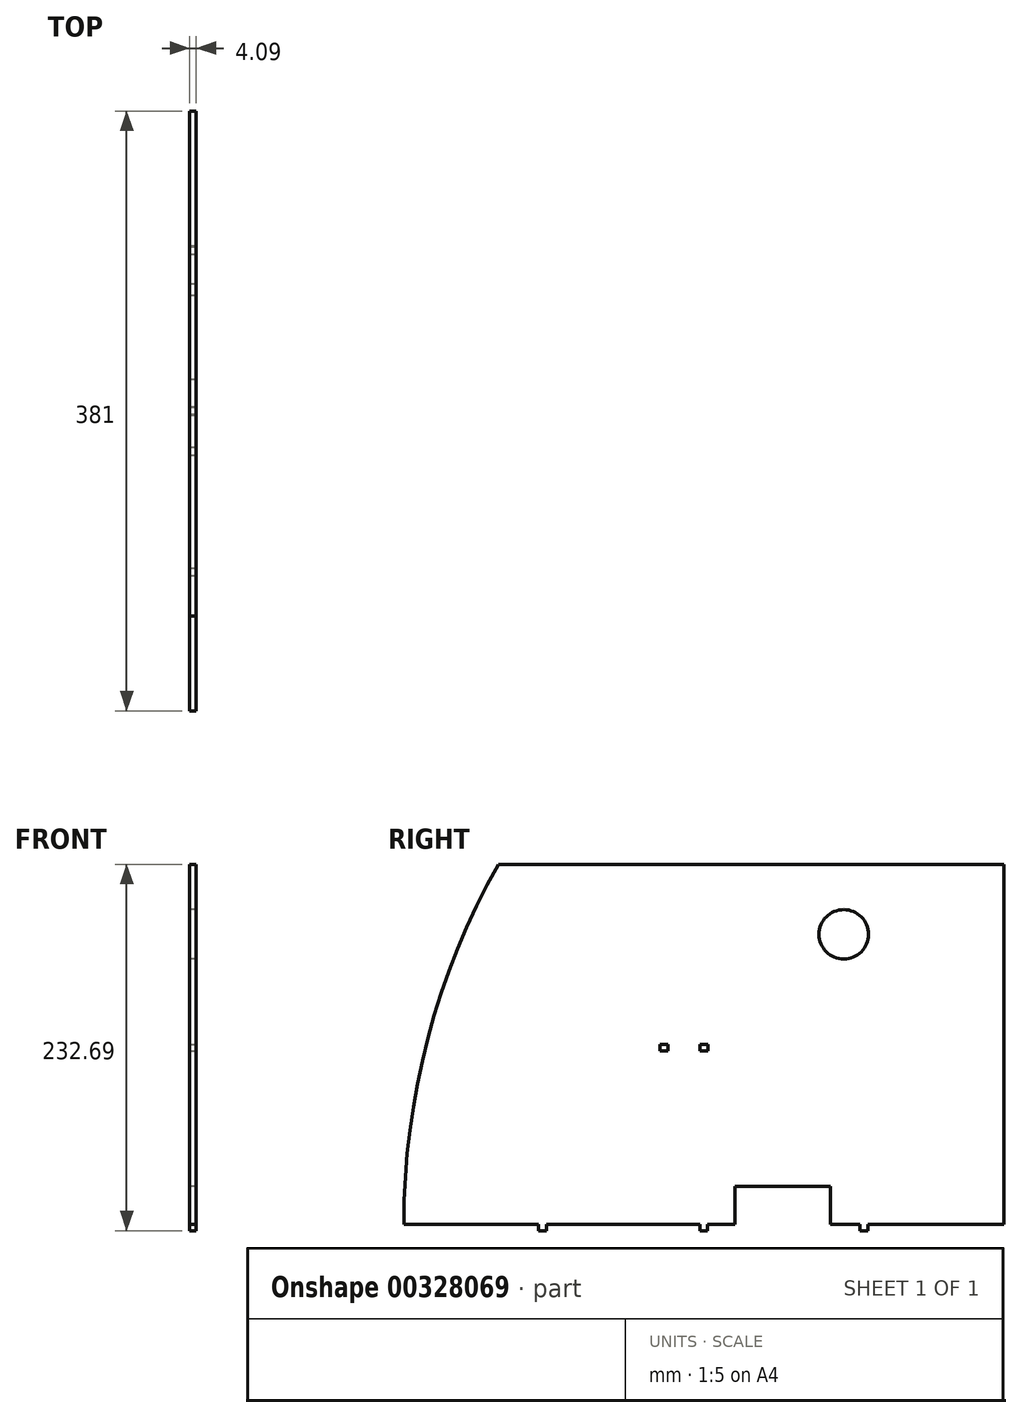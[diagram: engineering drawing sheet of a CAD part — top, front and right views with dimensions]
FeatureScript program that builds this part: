
annotation { "Feature Type Name" : "Feature", "Feature Type Description" : "" }
export const myFeature = defineFeature(function(context is Context, id is Id, definition is map)
    precondition{}
    {
        {
            var Q0;
            Q0=qCreatedBy(makeId("Right.planeOp"),FACE);
            var sketch = newSketch(context, id + "F0", { "sketchPlane" : qUnion([Q0])});
            skLineSegment(sketch, "E0.left", {"start": v(190.5, -228.6) * mm, "end": v(190.5, 0) * mm});
            skPoint(sketch, "E0.middle", {"position": v(0, 0) * mm});
            skArc(sketch, "E1", {"start": v(-130.4, 0) * mm, "mid": v(-175.22, -110.42) * mm, "end": v(-190.5, -228.6) * mm});
            skLineSegment(sketch, "E2", {"start": v(104.58, -44.45) * mm, "end": v(88.9, -44.45) * mm, "construction": true});
            skLineSegment(sketch, "E3", {"start": v(88.9, -44.45) * mm, "end": v(88.9, -60.13) * mm, "construction": true});
            skCircle(sketch, "E4", {"center": v(88.9, -44.45) * mm, "radius": 15.68 * mm});
            skPoint(sketch, "E0.top.end.orphan", {"position": v(-190.5, 228.6) * mm});
            skPoint(sketch, "E5.orphan", {"position": v(190.5, 228.6) * mm});
            skPoint(sketch, "E6.orphan", {"position": v(-0.8, -228.6) * mm});
            skPoint(sketch, "E7.start.orphan", {"position": v(0, -228.6) * mm});
            skLineSegment(sketch, "E8", {"start": v(-2.54, -228.6) * mm, "end": v(-190.5, -228.6) * mm});
            skLineSegment(sketch, "E9", {"start": v(-0.8, -228.6) * mm, "end": v(-102.4, -228.6) * mm, "construction": true});
            skLineSegment(sketch, "E10", {"start": v(-102.4, -228.6) * mm, "end": v(-102.4, -232.69) * mm, "construction": true});
            skLineSegment(sketch, "E11", {"start": v(190.5, -228.6) * mm, "end": v(104.38, -228.6) * mm});
            skLineSegment(sketch, "E12", {"start": v(2.54, -228.6) * mm, "end": v(19.8, -228.6) * mm, "construction": true});
            skLineSegment(sketch, "E13.trimOffspring", {"start": v(99.06, -228.6) * mm, "end": v(80.55, -228.6) * mm});
            skLineSegment(sketch, "E14", {"start": v(-102.4, -232.69) * mm, "end": v(-104.82, -232.69) * mm});
            skLineSegment(sketch, "E15", {"start": v(-102.4, -232.69) * mm, "end": v(-100, -232.69) * mm});
            skLineSegment(sketch, "E16", {"start": v(-104.82, -232.69) * mm, "end": v(-104.82, -228.6) * mm});
            skLineSegment(sketch, "E17", {"start": v(-100, -232.69) * mm, "end": v(-100, -228.6) * mm});
            skLineSegment(sketch, "E18", {"start": v(0, -228.6) * mm, "end": v(0, -232.69) * mm, "construction": true});
            skLineSegment(sketch, "E19", {"start": v(0, -232.69) * mm, "end": v(-2.41, -232.69) * mm});
            skLineSegment(sketch, "E20", {"start": v(0, -232.69) * mm, "end": v(2.41, -232.69) * mm});
            skLineSegment(sketch, "E21", {"start": v(-2.54, -228.6) * mm, "end": v(2.54, -228.6) * mm});
            skLineSegment(sketch, "E22", {"start": v(-2.41, -232.69) * mm, "end": v(-2.41, -228.6) * mm});
            skLineSegment(sketch, "E23", {"start": v(2.41, -232.69) * mm, "end": v(2.41, -228.6) * mm});
            skLineSegment(sketch, "E24", {"start": v(2.41, -228.6) * mm, "end": v(2.1, -228.63) * mm});
            skLineSegment(sketch, "E25", {"start": v(99.06, -228.6) * mm, "end": v(104.38, -228.6) * mm});
            skLineSegment(sketch, "E26", {"start": v(101.72, -228.6) * mm, "end": v(101.72, -232.69) * mm, "construction": true});
            skLineSegment(sketch, "E27", {"start": v(101.72, -232.69) * mm, "end": v(99.3, -232.69) * mm});
            skLineSegment(sketch, "E28", {"start": v(101.72, -232.69) * mm, "end": v(104.13, -232.69) * mm});
            skLineSegment(sketch, "E29", {"start": v(99.3, -232.69) * mm, "end": v(99.3, -228.6) * mm});
            skLineSegment(sketch, "E30", {"start": v(104.13, -232.69) * mm, "end": v(104.13, -228.6) * mm});
            skLineSegment(sketch, "E31", {"start": v(190.5, 0) * mm, "end": v(-130.4, 0) * mm});
            skLineSegment(sketch, "E32", {"start": v(88.9, -44.45) * mm, "end": v(190.5, -44.45) * mm, "construction": true});
            skLineSegment(sketch, "E33", {"start": v(0, -228.6) * mm, "end": v(0, 114.34) * mm, "construction": true});
            skLineSegment(sketch, "E34", {"start": v(88.9, -44.45) * mm, "end": v(0, -44.45) * mm, "construction": true});
            skLineSegment(sketch, "E35.top", {"start": v(19.8, -204.7) * mm, "end": v(80.55, -204.7) * mm});
            skLineSegment(sketch, "E35.left", {"start": v(19.8, -228.6) * mm, "end": v(19.8, -204.7) * mm});
            skLineSegment(sketch, "E35.right", {"start": v(80.55, -228.6) * mm, "end": v(80.55, -204.7) * mm});
            skLineSegment(sketch, "E36.trimOffspring", {"start": v(80.55, -228.6) * mm, "end": v(99.06, -228.6) * mm, "construction": true});
            skLineSegment(sketch, "E37.trimOffspring", {"start": v(19.8, -228.6) * mm, "end": v(2.54, -228.6) * mm});
            skSolve(sketch);
        }
        {
            var Q0;
            Q0 = qSketchRegion(id + "F0", true);
            extrude(context, id + "F1", {"entities" : qUnion([Q0]), "depth" : 4.1 * mm});
        }
        {
            var Q0;
            Q0=makeQuery(id+"F1.opExtrude","CAP_FACE",FACE,{"disambiguationData":[OSD([sQuery(id+"F0.wireOp",EDGE,"E1"),sQuery(id+"F0.wireOp",EDGE,"E4"),sQuery(id+"F0.wireOp",EDGE,"E8"),sQuery(id+"F0.wireOp",EDGE,"E11"),sQuery(id+"F0.wireOp",EDGE,"E13.trimOffspring"),sQuery(id+"F0.wireOp",EDGE,"E14"),sQuery(id+"F0.wireOp",EDGE,"E15"),sQuery(id+"F0.wireOp",EDGE,"E16"),sQuery(id+"F0.wireOp",EDGE,"E17"),sQuery(id+"F0.wireOp",EDGE,"E19"),sQuery(id+"F0.wireOp",EDGE,"E20"),sQuery(id+"F0.wireOp",EDGE,"E21"),sQuery(id+"F0.wireOp",EDGE,"E22"),sQuery(id+"F0.wireOp",EDGE,"E23"),sQuery(id+"F0.wireOp",EDGE,"E25"),sQuery(id+"F0.wireOp",EDGE,"E27"),sQuery(id+"F0.wireOp",EDGE,"E28"),sQuery(id+"F0.wireOp",EDGE,"E29"),sQuery(id+"F0.wireOp",EDGE,"E30"),sQuery(id+"F0.wireOp",EDGE,"E0.left"),sQuery(id+"F0.wireOp",EDGE,"E31"),sQuery(id+"F0.wireOp",EDGE,"E35.top"),sQuery(id+"F0.wireOp",EDGE,"E35.left"),sQuery(id+"F0.wireOp",EDGE,"E35.right"),sQuery(id+"F0.wireOp",EDGE,"E37.trimOffspring")])],"isStart":false});
            var sketch = newSketch(context, id + "F2", { "sketchPlane" : qUnion([Q0])});
            skLineSegment(sketch, "E38", {"start": v(0, -232.69) * mm, "end": v(0, 0) * mm, "construction": true});
            skLineSegment(sketch, "E39.bottom", {"start": v(2.54, -118.39) * mm, "end": v(-2.54, -118.39) * mm});
            skLineSegment(sketch, "E39.top", {"start": v(2.54, -114.3) * mm, "end": v(-2.54, -114.3) * mm});
            skLineSegment(sketch, "E39.left", {"start": v(2.54, -118.39) * mm, "end": v(2.54, -114.3) * mm});
            skLineSegment(sketch, "E39.right", {"start": v(-2.54, -118.39) * mm, "end": v(-2.54, -114.3) * mm});
            skPoint(sketch, "E39.middle", {"position": v(0, -116.34) * mm});
            skLineSegment(sketch, "E40", {"start": v(0, -116.34) * mm, "end": v(-25.4, -116.34) * mm, "construction": true});
            skLineSegment(sketch, "E41.bottom", {"start": v(-22.86, -118.39) * mm, "end": v(-27.94, -118.39) * mm});
            skLineSegment(sketch, "E41.top", {"start": v(-22.86, -114.3) * mm, "end": v(-27.94, -114.3) * mm});
            skLineSegment(sketch, "E41.left", {"start": v(-22.86, -118.39) * mm, "end": v(-22.86, -114.3) * mm});
            skLineSegment(sketch, "E41.right", {"start": v(-27.94, -118.39) * mm, "end": v(-27.94, -114.3) * mm});
            skPoint(sketch, "E41.middle", {"position": v(-25.4, -116.34) * mm});
            skSolve(sketch);
        }
        {
            var Q0;
            Q0 = qSketchRegion(id + "F2", true);
            extrude(context, id + "F3", {"entities" : qUnion([Q0]), "operationType" : NewBodyOperationType.REMOVE, "oppositeDirection" : true, "depth" : 25.4 * mm});
        }
    });
